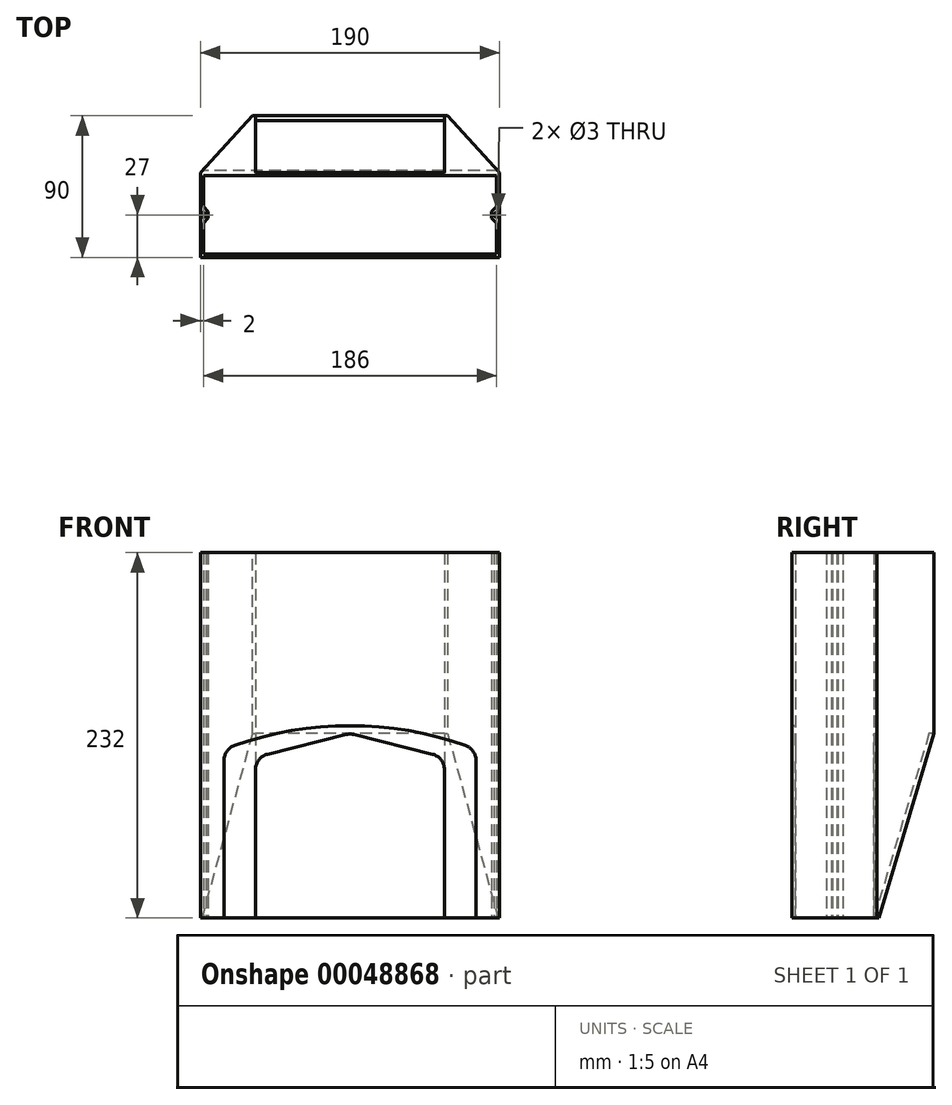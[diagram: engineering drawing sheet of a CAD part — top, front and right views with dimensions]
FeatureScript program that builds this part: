
annotation { "Feature Type Name" : "Feature", "Feature Type Description" : "" }
export const myFeature = defineFeature(function(context is Context, id is Id, definition is map)
    precondition{}
    {
        {
            var Q0;
            Q0=qCreatedBy(makeId("Top.planeOp"),FACE);
            var sketch = newSketch(context, id + "F0", { "sketchPlane" : qUnion([Q0])});
            skLineSegment(sketch, "E0.bottom", {"start": v(0, 0) * mm, "end": v(190, 0) * mm});
            skLineSegment(sketch, "E0.top", {"start": v(0, 54) * mm, "end": v(190, 54) * mm});
            skLineSegment(sketch, "E0.left", {"start": v(0, 0) * mm, "end": v(0, 54) * mm});
            skLineSegment(sketch, "E0.right", {"start": v(190, 0) * mm, "end": v(190, 54) * mm});
            skLineSegment(sketch, "E1.bottom", {"start": v(2, 2) * mm, "end": v(188, 2) * mm});
            skLineSegment(sketch, "E1.top", {"start": v(2, 52) * mm, "end": v(188, 52) * mm});
            skLineSegment(sketch, "E2", {"start": v(2, 52) * mm, "end": v(2, 32.12) * mm});
            skLineSegment(sketch, "E3", {"start": v(2, 32.12) * mm, "end": v(5, 29.12) * mm});
            skLineSegment(sketch, "E4", {"start": v(5, 29.12) * mm, "end": v(5, 24.88) * mm});
            skLineSegment(sketch, "E5", {"start": v(5, 24.88) * mm, "end": v(2, 21.88) * mm});
            skLineSegment(sketch, "E6", {"start": v(2, 21.88) * mm, "end": v(2, 2) * mm});
            skLineSegment(sketch, "E7", {"start": v(2, 32.12) * mm, "end": v(2, 21.88) * mm, "construction": true});
            skCircle(sketch, "E8", {"center": v(2, 27) * mm, "radius": 1.5 * mm});
            skLineSegment(sketch, "E9", {"start": v(95, 52) * mm, "end": v(95, 2) * mm, "construction": true});
            skLineSegment(sketch, "E10.MirrorCS", {"start": v(188, 21.88) * mm, "end": v(188, 2) * mm});
            skLineSegment(sketch, "E11.MirrorCS", {"start": v(185, 24.88) * mm, "end": v(188, 21.88) * mm});
            skLineSegment(sketch, "E12.MirrorCS", {"start": v(185, 29.12) * mm, "end": v(185, 24.88) * mm});
            skCircle(sketch, "E13.MirrorC", {"center": v(188, 27) * mm, "radius": 1.5 * mm});
            skLineSegment(sketch, "E14.MirrorCS", {"start": v(188, 52) * mm, "end": v(188, 32.12) * mm});
            skLineSegment(sketch, "E15.MirrorCS", {"start": v(188, 32.12) * mm, "end": v(185, 29.12) * mm});
            skSolve(sketch);
        }
        {
            var Q0;
            Q0=makeQuery(id+"F0.imprint","IMPRINT",FACE,{"disambiguationData":[TD([[makeQuery(id+"F0.imprint","IMPRINT",EDGE,{"derivedFrom":sQuery(id+"F0.wireOp",EDGE,"E0.bottom")}),1.0]])]});
            extrude(context, id + "F1", {"entities" : qUnion([Q0]), "depth" : 232 * mm});
        }
        {
            var Q0;
            Q0=makeQuery(id+"F1.opExtrude","SWEPT_FACE",FACE,{"disambiguationData":[OSD([sQuery(id+"F0.wireOp",EDGE,"E0.top")])]});
            var sketch = newSketch(context, id + "F2", { "sketchPlane" : qUnion([Q0])});
            skLineSegment(sketch, "E16.bottom", {"start": v(-35, 232) * mm, "end": v(-155, 232) * mm});
            skLineSegment(sketch, "E16.top", {"start": v(-35, 117) * mm, "end": v(-155, 117) * mm});
            skLineSegment(sketch, "E16.left", {"start": v(-35, 232) * mm, "end": v(-35, 117) * mm});
            skLineSegment(sketch, "E16.right", {"start": v(-155, 232) * mm, "end": v(-155, 117) * mm});
            skLineSegment(sketch, "E17", {"start": v(-35, 117) * mm, "end": v(-35, 23) * mm});
            skLineSegment(sketch, "E18", {"start": v(-155, 23) * mm, "end": v(-155, 117) * mm});
            skLineSegment(sketch, "E19", {"start": v(-35, 23) * mm, "end": v(-35, 0) * mm});
            skLineSegment(sketch, "E20", {"start": v(-155, 23) * mm, "end": v(-155, 0) * mm});
            skLineSegment(sketch, "E21", {"start": v(-35, 102) * mm, "end": v(-95, 117) * mm});
            skLineSegment(sketch, "E22", {"start": v(-95, 117) * mm, "end": v(-155, 102) * mm});
            skSolve(sketch);
        }
        {
            var Q0;
            {var subQ3=sQuery(id+"F2.wireOp",EDGE,"38e1e8e2-cc66-4617-a444-6c9ce9c8846c");Q0=makeQuery(id+"F2.imprint","IMPRINT",FACE,{"disambiguationData":[TD([[makeQuery(id+"F2.imprint","IMPRINT",EDGE,{"derivedFrom":subQ3}),-1.0]])]});}
            var Q1;
            {var subQ1=sQuery(id+"F2.wireOp",EDGE,"E19");Q1=makeQuery(id+"F2.imprint","IMPRINT",FACE,{"disambiguationData":[TD([[makeQuery(id+"F2.imprint","IMPRINT",EDGE,{"derivedFrom":subQ1}),-1.0]])]});}
            extrude(context, id + "F3", {"entities" : qUnion([Q0, Q1]), "operationType" : NewBodyOperationType.REMOVE, "oppositeDirection" : true, "depth" : 25 * mm});
        }
        {
            var Q0;
            {var subQ3=sQuery(id+"F2.wireOp",EDGE,"E16.left");Q0=makeQuery(id+"F2.imprint","IMPRINT",FACE,{"disambiguationData":[TD([[makeQuery(id+"F2.imprint","IMPRINT",EDGE,{"derivedFrom":subQ3}),1.0]])]});}
            var Q1;
            {var subQ3=sQuery(id+"F2.wireOp",EDGE,"E16.right");Q1=makeQuery(id+"F2.imprint","IMPRINT",FACE,{"disambiguationData":[TD([[makeQuery(id+"F2.imprint","IMPRINT",EDGE,{"derivedFrom":subQ3}),-1.0]])]});}
            var Q2;
            Q2=makeQuery(id+"F2.imprint","IMPRINT",FACE,{"disambiguationData":[TD([[makeQuery(id+"F2.imprint","IMPRINT",EDGE,{"derivedFrom":sQuery(id+"F2.wireOp",EDGE,"E17")}),1.0]])]});
            var Q3;
            Q3=makeQuery(id+"F2.imprint","IMPRINT",FACE,{"disambiguationData":[TD([[makeQuery(id+"F2.imprint","IMPRINT",EDGE,{"derivedFrom":sQuery(id+"F2.wireOp",EDGE,"E18")}),1.0]])]});
            extrude(context, id + "F4", {"entities" : qUnion([Q0, Q1, Q2, Q3]), "operationType" : NewBodyOperationType.ADD, "depth" : 36 * mm});
        }
        {
            var Q0;
            Q0=makeQuery(id+"F1.opExtrude","SWEPT_FACE",FACE,{"disambiguationData":[OSD([sQuery(id+"F0.wireOp",EDGE,"E0.bottom")])]});
            var sketch = newSketch(context, id + "F5", { "sketchPlane" : qUnion([Q0])});
            skLineSegment(sketch, "E23.bottom", {"start": v(175, 107) * mm, "end": v(15, 107) * mm});
            skLineSegment(sketch, "E23.top", {"start": v(175, 0) * mm, "end": v(15, 0) * mm});
            skLineSegment(sketch, "E23.left", {"start": v(175, 107) * mm, "end": v(175, 0) * mm});
            skLineSegment(sketch, "E23.right", {"start": v(15, 107) * mm, "end": v(15, 0) * mm});
            skArc(sketch, "E24", {"start": v(175, 107) * mm, "mid": v(95, 122) * mm, "end": v(15, 107) * mm});
            skSolve(sketch);
        }
        {
            var Q0;
            Q0 = qSketchRegion(id + "F5", true);
            extrude(context, id + "F6", {"entities" : qUnion([Q0]), "operationType" : NewBodyOperationType.REMOVE, "oppositeDirection" : true, "depth" : 5 * mm});
        }
        {
            var Q0;
            Q0=makeQuery(id+"F6.boolean.opBoolean","COPY",EDGE,{"derivedFrom":makeQuery(id+"F6.opExtrude","SWEPT_EDGE",EDGE,{"disambiguationData":[OSD([sQuery(id+"F5.wireOp",EDGE,"E23.bottom"),sQuery(id+"F5.wireOp",EDGE,"E23.right"),sQuery(id+"F5.wireOp",EDGE,"E24")])]})});
            var Q1;
            Q1=makeQuery(id+"F6.boolean.opBoolean","COPY",EDGE,{"derivedFrom":makeQuery(id+"F6.opExtrude","SWEPT_EDGE",EDGE,{"disambiguationData":[OSD([sQuery(id+"F5.wireOp",EDGE,"E23.bottom"),sQuery(id+"F5.wireOp",EDGE,"E23.left"),sQuery(id+"F5.wireOp",EDGE,"E24")])]})});
            var Q2;
            Q2=makeQuery(id+"F3.boolean.opBoolean","COPY",EDGE,{"derivedFrom":makeQuery(id+"F3.opExtrude","SWEPT_EDGE",EDGE,{"disambiguationData":[OSD([sQuery(id+"F2.wireOp",EDGE,"E17"),sQuery(id+"F2.wireOp",EDGE,"E21")])]})});
            var Q3;
            Q3=makeQuery(id+"F3.boolean.opBoolean","COPY",EDGE,{"derivedFrom":makeQuery(id+"F3.opExtrude","SWEPT_EDGE",EDGE,{"disambiguationData":[OSD([sQuery(id+"F2.wireOp",EDGE,"E18"),sQuery(id+"F2.wireOp",EDGE,"E22")])]})});
            var Q4;
            Q4=makeQuery(id+"F3.boolean.opBoolean","COPY",EDGE,{"derivedFrom":makeQuery(id+"F3.opExtrude","SWEPT_EDGE",EDGE,{"disambiguationData":[OSD([sQuery(id+"F2.wireOp",EDGE,"E16.top"),sQuery(id+"F2.wireOp",EDGE,"E21"),sQuery(id+"F2.wireOp",EDGE,"E22")])]})});
            fillet(context, id + "F7", {"entities" : qUnion([Q0, Q1, Q2, Q3, Q4]), "radius" : 10 * mm, "tangentPropagation" : true, "allowEdgeOverflow" : false});
        }
        {
            var Q0;
            Q0=makeQuery(id+"F4.opExtrude","CAP_EDGE",EDGE,{"disambiguationData":[OSD([sQuery(id+"F0.wireOp",EDGE,"E0.top"),sQuery(id+"F0.wireOp",EDGE,"E0.right")])],"isStart":false});
            chamfer(context, id + "F8", {"entities" : qUnion([Q0]), "chamferType" : ChamferType.TWO_OFFSETS, "width1" : 33 * mm, "oppositeDirection" : false, "width2" : 36 * mm, "tangentPropagation" : true});
        }
        {
            var Q0;
            Q0=makeQuery(id+"F4.opExtrude","CAP_EDGE",EDGE,{"disambiguationData":[OSD([sQuery(id+"F0.wireOp",EDGE,"E0.top"),sQuery(id+"F0.wireOp",EDGE,"E0.left")])],"isStart":false});
            chamfer(context, id + "F9", {"entities" : qUnion([Q0]), "chamferType" : ChamferType.TWO_OFFSETS, "width1" : 36 * mm, "oppositeDirection" : false, "width2" : 33 * mm, "tangentPropagation" : true});
        }
        {
            var Q0;
            {var subQ0=sQuery(id+"F2.wireOp",EDGE,"E19");var subQ1=sQuery(id+"F2.wireOp",EDGE,"E17");Q0=makeQuery(id+"F4.boolean.opBoolean","MERGE",FACE,{"derivedFrom":[makeQuery(id+"F3.boolean.opBoolean","COPY",FACE,{"derivedFrom":makeQuery(id+"F3.opExtrude","SWEPT_FACE",FACE,{"disambiguationData":[OSD([subQ1,subQ0])]})}),makeQuery(id+"F4.opExtrude","SWEPT_FACE",FACE,{"disambiguationData":[OSD([sQuery(id+"F2.wireOp",EDGE,"E16.left"),subQ1,subQ0])]})]});}
            var sketch = newSketch(context, id + "F10", { "sketchPlane" : qUnion([Q0])});
            skLineSegment(sketch, "E25", {"start": v(90, 117) * mm, "end": v(87, 117) * mm});
            skLineSegment(sketch, "E26", {"start": v(87, 117) * mm, "end": v(52, 0) * mm});
            skLineSegment(sketch, "E27", {"start": v(90, 117) * mm, "end": v(55, 0) * mm});
            skSolve(sketch);
        }
        {
            var Q0;
            Q0 = qSketchRegion(id + "F10", true);
            var Q1;
            Q1=makeQuery(id+"F10.imprint","IMPRINT",FACE,{"disambiguationData":[TD([[makeQuery(id+"F10.imprint","IMPRINT",EDGE,{"derivedFrom":sQuery(id+"F10.wireOp",EDGE,"E25")}),1.0]])]});
            extrude(context, id + "F11", {"entities" : qUnion([Q0, Q1]), "operationType" : NewBodyOperationType.ADD, "depth" : 120 * mm});
        }
        {
            var Q0;
            Q0 = qSketchRegion(id + "F10", true);
            var Q1;
            {var subQ0=sQuery(id+"F2.wireOp",EDGE,"E19");var subQ1=sQuery(id+"F2.wireOp",EDGE,"E17");var subQ2=sQuery(id+"F2.wireOp",EDGE,"E16.left");var subQ3=sQuery(id+"F0.wireOp",EDGE,"E0.left");var subQ4=sQuery(id+"F0.wireOp",EDGE,"E0.top");var subQ5=makeQuery(id+"F1.opExtrude","CAP_EDGE",EDGE,{"disambiguationData":[OSD([subQ4])],"isStart":true});var subQ6=makeQuery(id+"F3.boolean.opBoolean","COPY",FACE,{"derivedFrom":makeQuery(id+"F3.opExtrude","SWEPT_FACE",FACE,{"disambiguationData":[OSD([subQ1,subQ0])]})});var subQ7=makeQuery(id+"F4.opExtrude","SWEPT_FACE",FACE,{"disambiguationData":[OSD([subQ2,subQ1,subQ0])]});var subQ8=sQuery(id+"F0.wireOp",EDGE,"E0.right");Q1=makeQuery(id+"F11.boolean.opBoolean","SPLIT",FACE,{"disambiguationData":[TD([makeQuery(id+"F1.opExtrude","CAP_FACE",FACE,{"disambiguationData":[OSD([sQuery(id+"F0.wireOp",EDGE,"E0.bottom"),subQ4,subQ3,subQ8,sQuery(id+"F0.wireOp",EDGE,"E1.bottom"),sQuery(id+"F0.wireOp",EDGE,"E1.top"),sQuery(id+"F0.wireOp",EDGE,"E2"),sQuery(id+"F0.wireOp",EDGE,"E3"),sQuery(id+"F0.wireOp",EDGE,"E4"),sQuery(id+"F0.wireOp",EDGE,"E5"),sQuery(id+"F0.wireOp",EDGE,"E6"),sQuery(id+"F0.wireOp",EDGE,"E8"),sQuery(id+"F0.wireOp",EDGE,"E10.MirrorCS"),sQuery(id+"F0.wireOp",EDGE,"E11.MirrorCS"),sQuery(id+"F0.wireOp",EDGE,"E12.MirrorCS"),sQuery(id+"F0.wireOp",EDGE,"E13.MirrorC"),sQuery(id+"F0.wireOp",EDGE,"E14.MirrorCS"),sQuery(id+"F0.wireOp",EDGE,"E15.MirrorCS")])],"isStart":true}),subQ6,subQ7,makeQuery(id+"F4.opExtrude","CAP_FACE",FACE,{"disambiguationData":[OSD([subQ4,subQ3,subQ2,subQ1,subQ0])],"isStart":false}),makeQuery(id+"F4.opExtrude","SWEPT_FACE",FACE,{"disambiguationData":[OSD([subQ4]),TDD([makeQuery(id+"F2.imprint","IMPRINT",EDGE,{"disambiguationData":[TD([[makeQuery(id+"F2.imprint","INTERSECT",VERTEX,{"derivedFrom":[subQ5,subQ0]}),1.0]])],"derivedFrom":subQ5})])]}),makeQuery(id+"F4.opExtrude","SWEPT_FACE",FACE,{"disambiguationData":[OSD([subQ4]),TDD([makeQuery(id+"F2.imprint","IMPRINT",EDGE,{"disambiguationData":[TD([[makeQuery(id+"F2.imprint","INTERSECT",VERTEX,{"derivedFrom":[subQ5,sQuery(id+"F2.wireOp",EDGE,"E20")]}),-1.0]])],"derivedFrom":subQ5})])]}),makeQuery(id+"F11.opExtrude","SWEPT_FACE",FACE,{"disambiguationData":[OSD([sQuery(id+"F10.wireOp",EDGE,"E25")])]}),makeQuery(id+"F11.opExtrude","SWEPT_FACE",FACE,{"disambiguationData":[OSD([sQuery(id+"F10.wireOp",EDGE,"E27")])]}),makeQuery(id+"F11.opExtrude","SWEPT_FACE",FACE,{"disambiguationData":[OSD([subQ4,subQ0])]})])],"derivedFrom":makeQuery(id+"F4.boolean.opBoolean","MERGE",FACE,{"derivedFrom":[subQ6,subQ7]})});}
            extrude(context, id + "F12", {"entities" : qUnion([Q0, Q1]), "operationType" : NewBodyOperationType.REMOVE, "oppositeDirection" : true, "depth" : 55 * mm, "hasSecondDirection" : true, "secondDirectionOppositeDirection" : false, "secondDirectionDepth" : 175 * mm});
        }
    });
